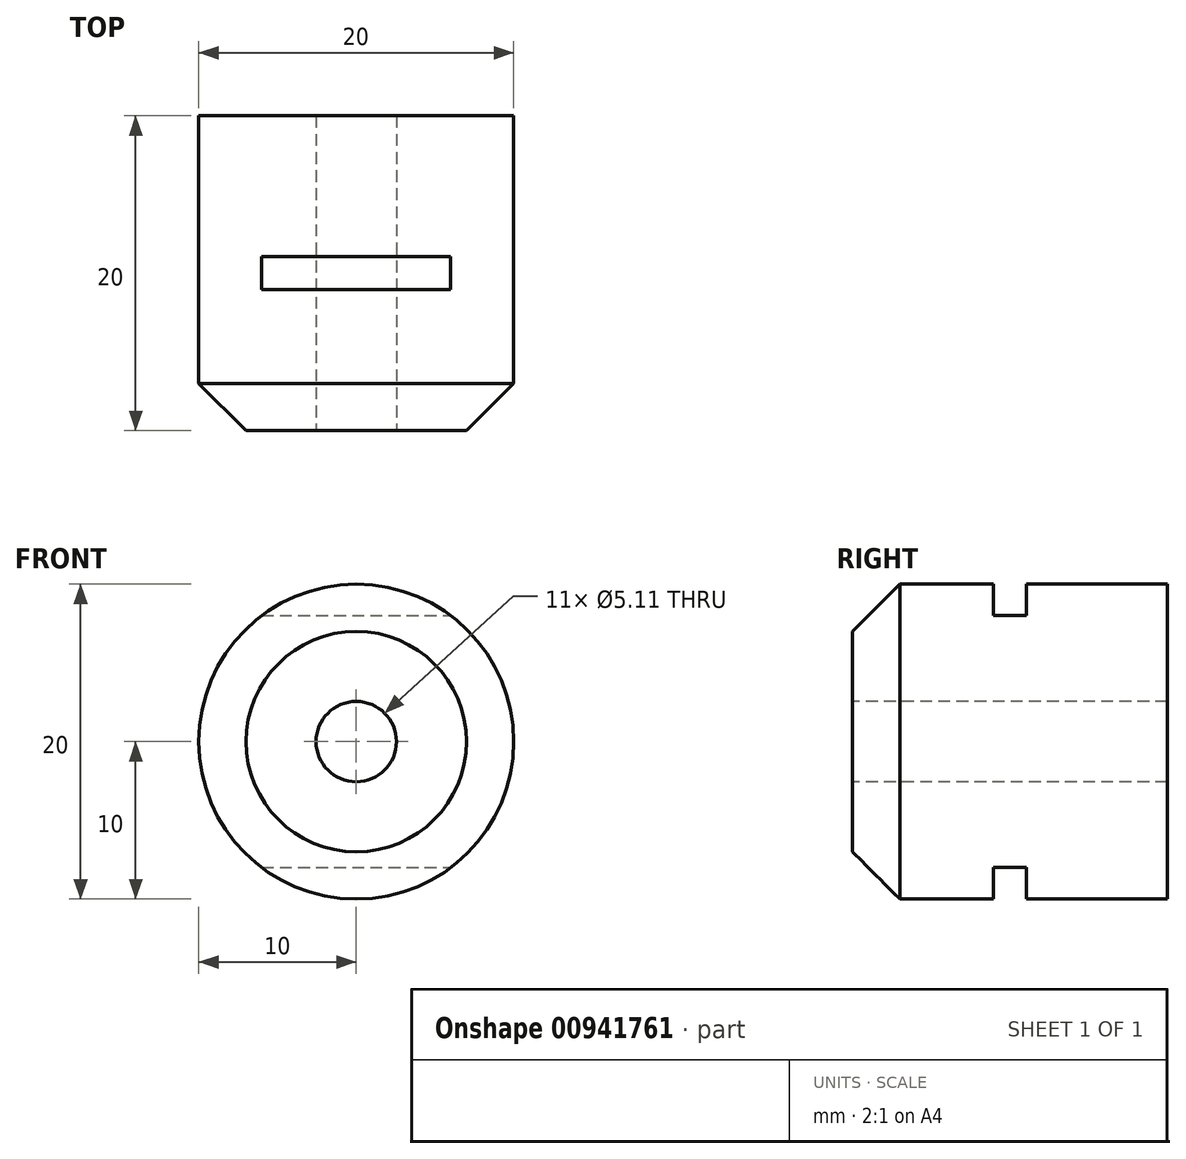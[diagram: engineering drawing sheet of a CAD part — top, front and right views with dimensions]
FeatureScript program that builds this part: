
annotation { "Feature Type Name" : "Feature", "Feature Type Description" : "" }
export const myFeature = defineFeature(function(context is Context, id is Id, definition is map)
    precondition{}
    {
        {
            var Q0;
            Q0=qCreatedBy(makeId("Front.planeOp"),FACE);
            var sketch = newSketch(context, id + "F0", { "sketchPlane" : qUnion([Q0])});
            skCircle(sketch, "E0", {"center": v(0, 0) * mm, "radius": 10 * mm});
            skSolve(sketch);
        }
        {
            var Q0;
            Q0 = qSketchRegion(id + "F0", true);
            extrude(context, id + "F1", {"entities" : qUnion([Q0]), "depth" : 20 * mm, "offsetDistance" : 25 * mm});
        }
        {
            var Q0;
            Q0=makeQuery(id+"F1.opExtrude","CAP_FACE",FACE,{"disambiguationData":[OSD([sQuery(id+"F0.wireOp",EDGE,"E0")])],"isStart":false});
            var sketch = newSketch(context, id + "F2", { "sketchPlane" : qUnion([Q0])});
            skPoint(sketch, "E1", {"position": v(0, 0) * mm});
            skSolve(sketch);
        }
        {
            var Q0;
            Q0=sQuery(id+"F2.wireOp",VERTEX,"E1");
            var Q1;
            Q1=makeQuery(id+"F1.opExtrude","SWEPT_BODY",BODY,{"disambiguationData":[OSD([sQuery(id+"F0.wireOp",EDGE,"E0")])]});
            hole(context, id + "F3", {"style" : HoleStyle.SIMPLE, "endStyle" : HoleEndStyle.THROUGH, "standardTappedOrClearance" : lookupTablePath({ "standard" : "ANSI", "engagement" : "75%", "pitch" : "20 tpi", "size" : "1/4", "type" : "Tapped" }), "standardBlindInLast" : lookupTablePath({ "standard" : "ANSI", "fit" : "Normal", "engagement" : "75%", "pitch" : "20 tpi", "size" : "1/4", "type" : "Clearance & tapped" }), "holeDiameter" : 5.1 * mm, "majorDiameter" : 6.35 * mm, "showTappedDepth" : true, "isTappedThrough" : true, "tappedDepth" : 12 * mm, "tapClearance" : 3, "startFromSketch" : true, "locations" : qUnion([Q0]), "scope" : qUnion([Q1])});
        }
        {
            var Q0;
            Q0=qCreatedBy(makeId("Right.planeOp"),FACE);
            var sketch = newSketch(context, id + "F4", { "sketchPlane" : qUnion([Q0])});
            skLineSegment(sketch, "E2.bottom", {"start": v(-11.05, 27.51) * mm, "end": v(-8.95, 27.51) * mm});
            skLineSegment(sketch, "E2.top", {"start": v(-11.05, 8) * mm, "end": v(-8.95, 8) * mm});
            skLineSegment(sketch, "E2.left", {"start": v(-11.05, 27.51) * mm, "end": v(-11.05, 8) * mm});
            skLineSegment(sketch, "E2.right", {"start": v(-8.95, 27.51) * mm, "end": v(-8.95, 8) * mm});
            skLineSegment(sketch, "E3", {"start": v(-10, 8) * mm, "end": v(-10, 27.51) * mm, "construction": true});
            skLineSegment(sketch, "E4", {"start": v(-20, 8) * mm, "end": v(0, 8) * mm, "construction": true});
            skLineSegment(sketch, "E5.MirrorCS", {"start": v(-8.95, -27.51) * mm, "end": v(-8.95, -8) * mm});
            skLineSegment(sketch, "E6.MirrorCS", {"start": v(-11.05, -27.51) * mm, "end": v(-8.95, -27.51) * mm});
            skLineSegment(sketch, "E7.MirrorCS", {"start": v(-20, -8) * mm, "end": v(0, -8) * mm, "construction": true});
            skLineSegment(sketch, "E8.MirrorCS", {"start": v(-11.05, -27.51) * mm, "end": v(-11.05, -8) * mm});
            skLineSegment(sketch, "E9", {"start": v(-8.95, -8) * mm, "end": v(-11.05, -8) * mm});
            skSolve(sketch);
        }
        {
            var Q0;
            Q0 = qSketchRegion(id + "F4", true);
            extrude(context, id + "F5", {"entities" : qUnion([Q0]), "operationType" : NewBodyOperationType.REMOVE, "endBound" : BoundingType.SYMMETRIC, "oppositeDirection" : true, "depth" : 25 * mm, "offsetDistance" : 25 * mm});
        }
        {
            var Q0;
            Q0=makeQuery(id+"F1.opExtrude","CAP_EDGE",EDGE,{"disambiguationData":[OSD([sQuery(id+"F0.wireOp",EDGE,"E0")])],"isStart":false});
            chamfer(context, id + "F6", {"entities" : qUnion([Q0]), "width" : 3 * mm, "tangentPropagation" : true});
        }
    });
